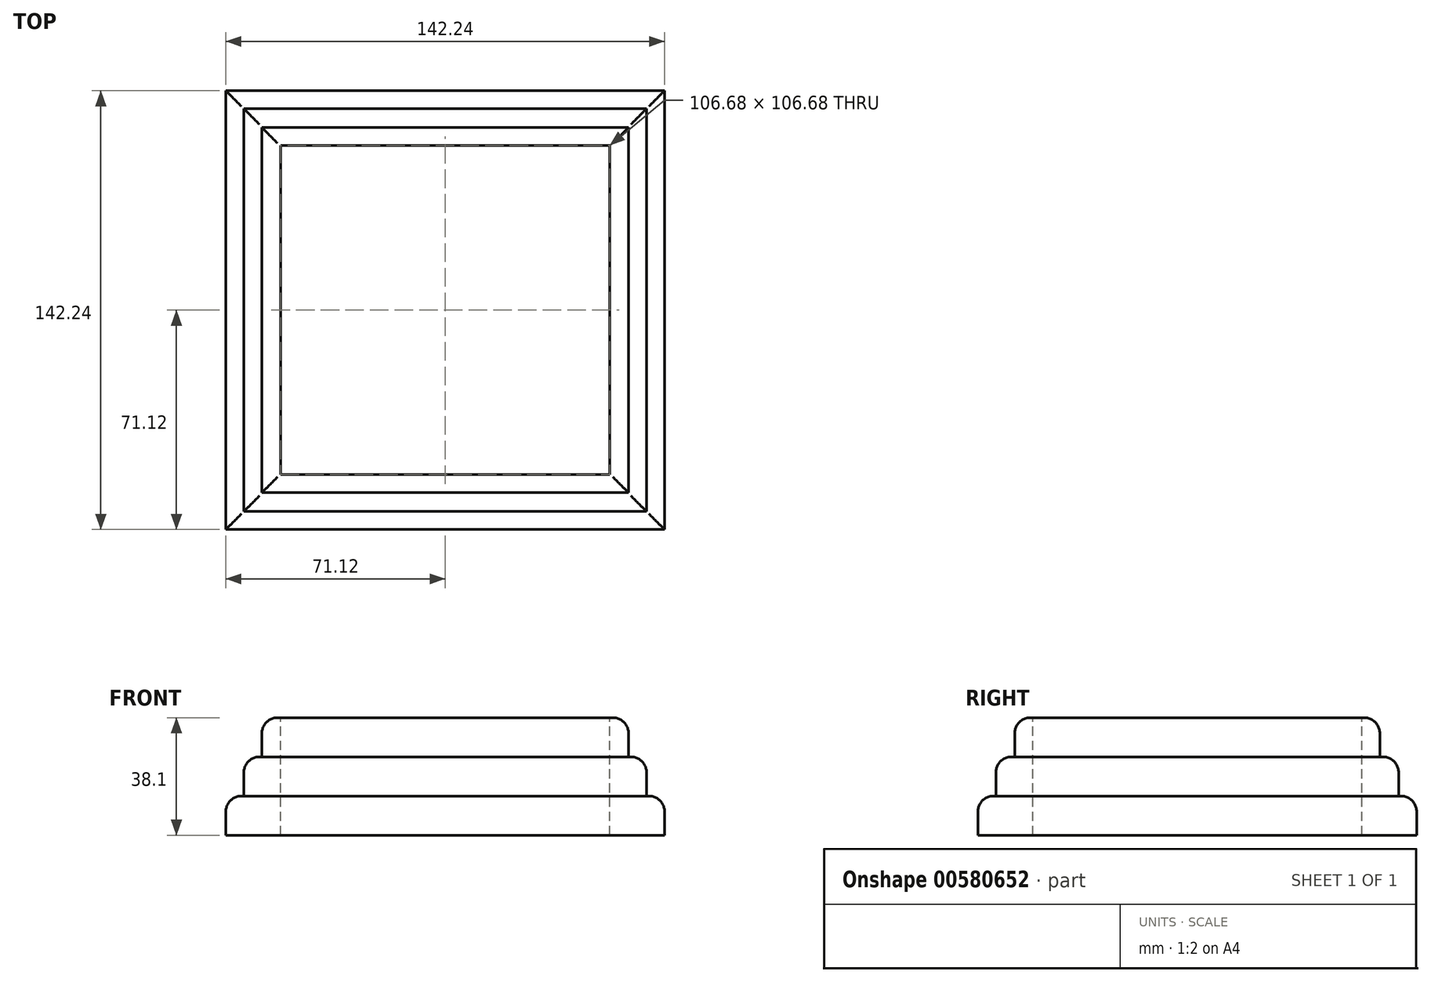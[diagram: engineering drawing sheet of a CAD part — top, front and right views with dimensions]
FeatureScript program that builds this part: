
annotation { "Feature Type Name" : "Feature", "Feature Type Description" : "" }
export const myFeature = defineFeature(function(context is Context, id is Id, definition is map)
    precondition{}
    {
        {
            var Q0;
            Q0=qCreatedBy(makeId("Top.planeOp"),FACE);
            var sketch = newSketch(context, id + "F0", { "sketchPlane" : qUnion([Q0])});
            skLineSegment(sketch, "E0.bottom", {"start": v(71.12, -71.12) * mm, "end": v(-71.12, -71.12) * mm});
            skLineSegment(sketch, "E0.top", {"start": v(71.12, 71.12) * mm, "end": v(-71.12, 71.12) * mm});
            skLineSegment(sketch, "E0.left", {"start": v(71.12, -71.12) * mm, "end": v(71.12, 71.12) * mm});
            skLineSegment(sketch, "E0.right", {"start": v(-71.12, -71.12) * mm, "end": v(-71.12, 71.12) * mm});
            skPoint(sketch, "E0.middle", {"position": v(0, 0) * mm});
            skSolve(sketch);
        }
        {
            var Q0;
            Q0=makeQuery(id+"F0.imprint","IMPRINT",FACE,{"disambiguationData":[TD([[makeQuery(id+"F0.imprint","IMPRINT",EDGE,{"derivedFrom":sQuery(id+"F0.wireOp",EDGE,"E0.bottom")}),-1.0]])]});
            extrude(context, id + "F1", {"entities" : qUnion([Q0]), "depth" : 12.7 * mm, "offsetDistance" : 25.4 * mm});
        }
        {
            var Q0;
            Q0=makeQuery(id+"F1.opExtrude","CAP_FACE",FACE,{"disambiguationData":[OSD([sQuery(id+"F0.wireOp",EDGE,"E0.bottom"),sQuery(id+"F0.wireOp",EDGE,"E0.top"),sQuery(id+"F0.wireOp",EDGE,"E0.left"),sQuery(id+"F0.wireOp",EDGE,"E0.right")])],"isStart":false});
            var sketch = newSketch(context, id + "F2", { "sketchPlane" : qUnion([Q0])});
            skLineSegment(sketch, "E1.bottom", {"start": v(53.34, -53.34) * mm, "end": v(-53.34, -53.34) * mm});
            skLineSegment(sketch, "E1.top", {"start": v(53.34, 53.34) * mm, "end": v(-53.34, 53.34) * mm});
            skLineSegment(sketch, "E1.left", {"start": v(53.34, -53.34) * mm, "end": v(53.34, 53.34) * mm});
            skLineSegment(sketch, "E1.right", {"start": v(-53.34, -53.34) * mm, "end": v(-53.34, 53.34) * mm});
            skPoint(sketch, "E1.middle", {"position": v(0, 0) * mm});
            skSolve(sketch);
        }
        {
            var Q0;
            Q0=makeQuery(id+"F2.imprint","IMPRINT",FACE,{"disambiguationData":[TD([[makeQuery(id+"F2.imprint","IMPRINT",EDGE,{"derivedFrom":sQuery(id+"F2.wireOp",EDGE,"E1.bottom")}),-1.0]])]});
            extrude(context, id + "F3", {"entities" : qUnion([Q0]), "operationType" : NewBodyOperationType.REMOVE, "endBound" : BoundingType.THROUGH_ALL, "oppositeDirection" : true, "depth" : 25.4 * mm, "offsetDistance" : 25.4 * mm});
        }
        {
            var Q0;
            Q0=makeQuery(id+"F1.opExtrude","CAP_FACE",FACE,{"disambiguationData":[OSD([sQuery(id+"F0.wireOp",EDGE,"E0.bottom"),sQuery(id+"F0.wireOp",EDGE,"E0.top"),sQuery(id+"F0.wireOp",EDGE,"E0.left"),sQuery(id+"F0.wireOp",EDGE,"E0.right")])],"isStart":false});
            var sketch = newSketch(context, id + "F4", { "sketchPlane" : qUnion([Q0])});
            skLineSegment(sketch, "E2.bottom", {"start": v(-65.28, -65.28) * mm, "end": v(65.28, -65.28) * mm});
            skLineSegment(sketch, "E2.top", {"start": v(-65.28, 65.28) * mm, "end": v(65.28, 65.28) * mm});
            skLineSegment(sketch, "E2.left", {"start": v(-65.28, -65.28) * mm, "end": v(-65.28, 65.28) * mm});
            skLineSegment(sketch, "E2.right", {"start": v(65.28, -65.28) * mm, "end": v(65.28, 65.28) * mm});
            skPoint(sketch, "E2.middle", {"position": v(0, 0) * mm});
            skSolve(sketch);
        }
        {
            var Q0;
            Q0=makeQuery(id+"F4.imprint","IMPRINT",FACE,{"disambiguationData":[TD([[makeQuery(id+"F4.imprint","IMPRINT",EDGE,{"derivedFrom":sQuery(id+"F4.wireOp",EDGE,"E2.bottom")}),1.0]])]});
            extrude(context, id + "F5", {"entities" : qUnion([Q0]), "operationType" : NewBodyOperationType.ADD, "depth" : 12.7 * mm, "offsetDistance" : 25.4 * mm});
        }
        {
            var Q0;
            Q0=makeQuery(id+"F5.opExtrude","CAP_FACE",FACE,{"disambiguationData":[OSD([sQuery(id+"F2.wireOp",EDGE,"E1.bottom"),sQuery(id+"F2.wireOp",EDGE,"E1.top"),sQuery(id+"F2.wireOp",EDGE,"E1.left"),sQuery(id+"F2.wireOp",EDGE,"E1.right"),sQuery(id+"F4.wireOp",EDGE,"E2.bottom"),sQuery(id+"F4.wireOp",EDGE,"E2.top"),sQuery(id+"F4.wireOp",EDGE,"E2.left"),sQuery(id+"F4.wireOp",EDGE,"E2.right")])],"isStart":false});
            var sketch = newSketch(context, id + "F6", { "sketchPlane" : qUnion([Q0])});
            skLineSegment(sketch, "E3.bottom", {"start": v(-59.44, 59.18) * mm, "end": v(59.44, 59.18) * mm});
            skLineSegment(sketch, "E3.top", {"start": v(-59.44, -59.18) * mm, "end": v(59.44, -59.18) * mm});
            skLineSegment(sketch, "E3.left", {"start": v(-59.44, 59.18) * mm, "end": v(-59.44, -59.18) * mm});
            skLineSegment(sketch, "E3.right", {"start": v(59.44, 59.18) * mm, "end": v(59.44, -59.18) * mm});
            skPoint(sketch, "E3.middle", {"position": v(0, 0) * mm});
            skSolve(sketch);
        }
        {
            var Q0;
            Q0=makeQuery(id+"F6.imprint","IMPRINT",FACE,{"disambiguationData":[TD([[makeQuery(id+"F6.imprint","IMPRINT",EDGE,{"derivedFrom":sQuery(id+"F6.wireOp",EDGE,"E3.bottom")}),-1.0]])]});
            extrude(context, id + "F7", {"entities" : qUnion([Q0]), "operationType" : NewBodyOperationType.ADD, "depth" : 12.7 * mm, "offsetDistance" : 25.4 * mm});
        }
        {
            var Q0;
            Q0=makeQuery(id+"F7.opExtrude","CAP_EDGE",EDGE,{"disambiguationData":[OSD([sQuery(id+"F6.wireOp",EDGE,"E3.top")])],"isStart":false});
            var Q1;
            Q1=makeQuery(id+"F7.opExtrude","CAP_EDGE",EDGE,{"disambiguationData":[OSD([sQuery(id+"F6.wireOp",EDGE,"E3.left")])],"isStart":false});
            var Q2;
            Q2=makeQuery(id+"F5.opExtrude","CAP_EDGE",EDGE,{"disambiguationData":[OSD([sQuery(id+"F4.wireOp",EDGE,"E2.bottom")])],"isStart":false});
            var Q3;
            Q3=makeQuery(id+"F1.opExtrude","CAP_EDGE",EDGE,{"disambiguationData":[OSD([sQuery(id+"F0.wireOp",EDGE,"E0.bottom")])],"isStart":false});
            var Q4;
            Q4=makeQuery(id+"F1.opExtrude","CAP_EDGE",EDGE,{"disambiguationData":[OSD([sQuery(id+"F0.wireOp",EDGE,"E0.right")])],"isStart":false});
            var Q5;
            Q5=makeQuery(id+"F5.opExtrude","CAP_EDGE",EDGE,{"disambiguationData":[OSD([sQuery(id+"F4.wireOp",EDGE,"E2.left")])],"isStart":false});
            var Q6;
            Q6=makeQuery(id+"F1.opExtrude","CAP_EDGE",EDGE,{"disambiguationData":[OSD([sQuery(id+"F0.wireOp",EDGE,"E0.top")])],"isStart":false});
            var Q7;
            Q7=makeQuery(id+"F5.opExtrude","CAP_EDGE",EDGE,{"disambiguationData":[OSD([sQuery(id+"F4.wireOp",EDGE,"E2.top")])],"isStart":false});
            var Q8;
            Q8=makeQuery(id+"F7.opExtrude","CAP_EDGE",EDGE,{"disambiguationData":[OSD([sQuery(id+"F6.wireOp",EDGE,"E3.bottom")])],"isStart":false});
            var Q9;
            Q9=makeQuery(id+"F7.opExtrude","CAP_EDGE",EDGE,{"disambiguationData":[OSD([sQuery(id+"F6.wireOp",EDGE,"E3.right")])],"isStart":false});
            var Q10;
            Q10=makeQuery(id+"F5.opExtrude","CAP_EDGE",EDGE,{"disambiguationData":[OSD([sQuery(id+"F4.wireOp",EDGE,"E2.right")])],"isStart":false});
            var Q11;
            Q11=makeQuery(id+"F1.opExtrude","CAP_EDGE",EDGE,{"disambiguationData":[OSD([sQuery(id+"F0.wireOp",EDGE,"E0.left")])],"isStart":false});
            fillet(context, id + "F8", {"entities" : qUnion([Q0, Q1, Q2, Q3, Q4, Q5, Q6, Q7, Q8, Q9, Q10, Q11]), "radius" : 5.08 * mm, "tangentPropagation" : true, "allowEdgeOverflow" : false});
        }
    });
